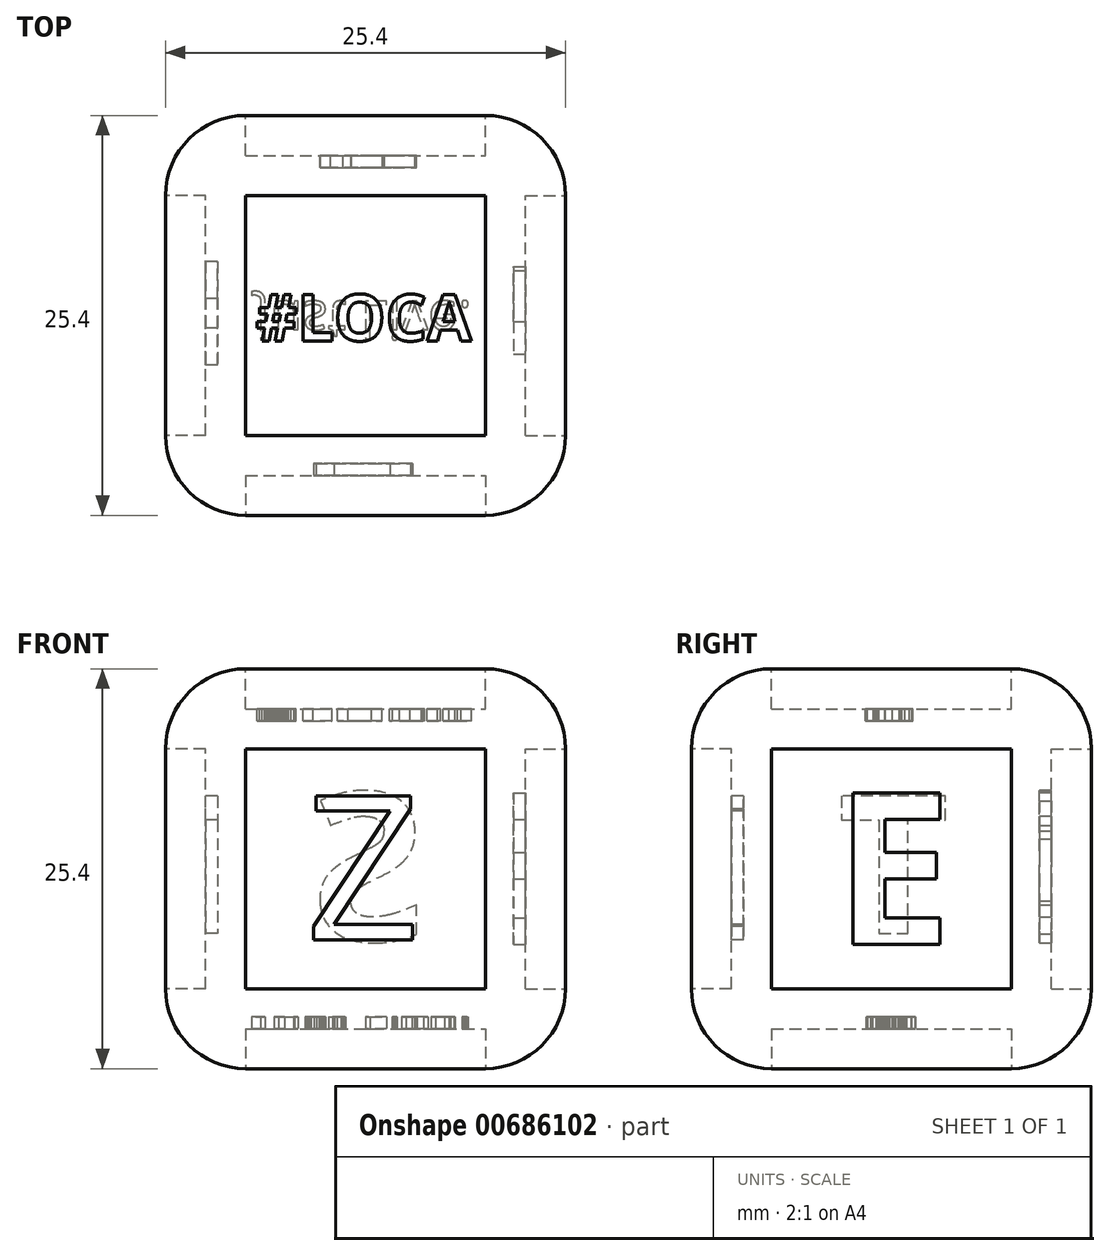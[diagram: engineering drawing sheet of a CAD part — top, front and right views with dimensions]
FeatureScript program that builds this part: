
annotation { "Feature Type Name" : "Feature", "Feature Type Description" : "" }
export const myFeature = defineFeature(function(context is Context, id is Id, definition is map)
    precondition{}
    {
        {
            var Q0;
            Q0=qCreatedBy(makeId("Front.planeOp"),FACE);
            var sketch = newSketch(context, id + "F0", { "sketchPlane" : qUnion([Q0])});
            skLineSegment(sketch, "E0.bottom", {"start": v(-12.7, -12.7) * mm, "end": v(12.7, -12.7) * mm});
            skLineSegment(sketch, "E0.top", {"start": v(-12.7, 12.7) * mm, "end": v(12.7, 12.7) * mm});
            skLineSegment(sketch, "E0.left", {"start": v(-12.7, -12.7) * mm, "end": v(-12.7, 12.7) * mm});
            skLineSegment(sketch, "E0.right", {"start": v(12.7, -12.7) * mm, "end": v(12.7, 12.7) * mm});
            skPoint(sketch, "E0.middle", {"position": v(0, 0) * mm});
            skSolve(sketch);
        }
        {
            var Q0;
            Q0=makeQuery(id+"F0.imprint","IMPRINT",FACE,{"disambiguationData":[TD([[makeQuery(id+"F0.imprint","IMPRINT",EDGE,{"derivedFrom":sQuery(id+"F0.wireOp",EDGE,"E0.bottom")}),1.0]])]});
            extrude(context, id + "F1", {"entities" : qUnion([Q0]), "depth" : 25.4 * mm, "offsetDistance" : 25.4 * mm});
        }
        {
            var Q0;
            Q0=makeQuery(id+"F1.opExtrude","CAP_FACE",FACE,{"disambiguationData":[OSD([sQuery(id+"F0.wireOp",EDGE,"E0.bottom"),sQuery(id+"F0.wireOp",EDGE,"E0.top"),sQuery(id+"F0.wireOp",EDGE,"E0.left"),sQuery(id+"F0.wireOp",EDGE,"E0.right")])],"isStart":false});
            var Q1;
            Q1=makeQuery(id+"F1.opExtrude","SWEPT_FACE",FACE,{"disambiguationData":[OSD([sQuery(id+"F0.wireOp",EDGE,"E0.right")])]});
            var Q2;
            Q2=makeQuery(id+"F1.opExtrude","SWEPT_FACE",FACE,{"disambiguationData":[OSD([sQuery(id+"F0.wireOp",EDGE,"E0.top")])]});
            var Q3;
            Q3=makeQuery(id+"F1.opExtrude","CAP_FACE",FACE,{"disambiguationData":[OSD([sQuery(id+"F0.wireOp",EDGE,"E0.bottom"),sQuery(id+"F0.wireOp",EDGE,"E0.top"),sQuery(id+"F0.wireOp",EDGE,"E0.left"),sQuery(id+"F0.wireOp",EDGE,"E0.right")])],"isStart":true});
            var Q4;
            Q4=makeQuery(id+"F1.opExtrude","SWEPT_FACE",FACE,{"disambiguationData":[OSD([sQuery(id+"F0.wireOp",EDGE,"E0.bottom")])]});
            var Q5;
            Q5=makeQuery(id+"F1.opExtrude","SWEPT_FACE",FACE,{"disambiguationData":[OSD([sQuery(id+"F0.wireOp",EDGE,"E0.left")])]});
            fillet(context, id + "F2", {"entities" : qUnion([Q0, Q1, Q2, Q3, Q4, Q5]), "radius" : 5.08 * mm, "tangentPropagation" : true, "allowEdgeOverflow" : false});
        }
        {
            var Q0;
            Q0=makeQuery(id+"F1.opExtrude","CAP_FACE",FACE,{"disambiguationData":[OSD([sQuery(id+"F0.wireOp",EDGE,"E0.bottom"),sQuery(id+"F0.wireOp",EDGE,"E0.top"),sQuery(id+"F0.wireOp",EDGE,"E0.left"),sQuery(id+"F0.wireOp",EDGE,"E0.right")])],"isStart":false});
            extrude(context, id + "F3", {"entities" : qUnion([Q0]), "operationType" : NewBodyOperationType.REMOVE, "oppositeDirection" : true, "depth" : 2.54 * mm, "offsetDistance" : 25.4 * mm});
        }
        {
            var Q0;
            Q0=makeQuery(id+"F1.opExtrude","SWEPT_FACE",FACE,{"disambiguationData":[OSD([sQuery(id+"F0.wireOp",EDGE,"E0.right")])]});
            extrude(context, id + "F4", {"entities" : qUnion([Q0]), "operationType" : NewBodyOperationType.REMOVE, "oppositeDirection" : true, "depth" : 2.54 * mm, "offsetDistance" : 25.4 * mm});
        }
        {
            var Q0;
            Q0=makeQuery(id+"F1.opExtrude","SWEPT_FACE",FACE,{"disambiguationData":[OSD([sQuery(id+"F0.wireOp",EDGE,"E0.top")])]});
            extrude(context, id + "F5", {"entities" : qUnion([Q0]), "operationType" : NewBodyOperationType.ADD, "depth" : 2.54 * mm, "offsetDistance" : 25.4 * mm});
        }
        {
            var Q0;
            Q0=makeQuery(id+"F5.opExtrude","CAP_FACE",FACE,{"disambiguationData":[OSD([sQuery(id+"F0.wireOp",EDGE,"E0.top")])],"isStart":false});
            extrude(context, id + "F6", {"entities" : qUnion([Q0]), "operationType" : NewBodyOperationType.REMOVE, "oppositeDirection" : true, "depth" : 5.08 * mm, "offsetDistance" : 25.4 * mm});
        }
        {
            var Q0;
            Q0=makeQuery(id+"F1.opExtrude","SWEPT_FACE",FACE,{"disambiguationData":[OSD([sQuery(id+"F0.wireOp",EDGE,"E0.bottom")])]});
            extrude(context, id + "F7", {"entities" : qUnion([Q0]), "operationType" : NewBodyOperationType.REMOVE, "oppositeDirection" : true, "depth" : 2.54 * mm, "offsetDistance" : 25.4 * mm});
        }
        {
            var Q0;
            Q0=makeQuery(id+"F1.opExtrude","CAP_FACE",FACE,{"disambiguationData":[OSD([sQuery(id+"F0.wireOp",EDGE,"E0.bottom"),sQuery(id+"F0.wireOp",EDGE,"E0.top"),sQuery(id+"F0.wireOp",EDGE,"E0.left"),sQuery(id+"F0.wireOp",EDGE,"E0.right")])],"isStart":true});
            extrude(context, id + "F8", {"entities" : qUnion([Q0]), "operationType" : NewBodyOperationType.ADD, "depth" : 2.54 * mm, "offsetDistance" : 25.4 * mm});
        }
        {
            var Q0;
            Q0=makeQuery(id+"F8.opExtrude","CAP_FACE",FACE,{"disambiguationData":[OSD([sQuery(id+"F0.wireOp",EDGE,"E0.bottom"),sQuery(id+"F0.wireOp",EDGE,"E0.top"),sQuery(id+"F0.wireOp",EDGE,"E0.left"),sQuery(id+"F0.wireOp",EDGE,"E0.right")])],"isStart":false});
            extrude(context, id + "F9", {"entities" : qUnion([Q0]), "operationType" : NewBodyOperationType.REMOVE, "oppositeDirection" : true, "depth" : 5.08 * mm, "offsetDistance" : 25.4 * mm});
        }
        {
            var Q0;
            Q0=makeQuery(id+"F1.opExtrude","SWEPT_FACE",FACE,{"disambiguationData":[OSD([sQuery(id+"F0.wireOp",EDGE,"E0.left")])]});
            extrude(context, id + "F10", {"entities" : qUnion([Q0]), "operationType" : NewBodyOperationType.REMOVE, "oppositeDirection" : true, "depth" : 2.54 * mm, "offsetDistance" : 25.4 * mm});
        }
        {
            var Q0;
            Q0=makeQuery(id+"F3.boolean.opBoolean","COPY",FACE,{"derivedFrom":makeQuery(id+"F3.opExtrude","CAP_FACE",FACE,{"disambiguationData":[OSD([sQuery(id+"F0.wireOp",EDGE,"E0.bottom"),sQuery(id+"F0.wireOp",EDGE,"E0.top"),sQuery(id+"F0.wireOp",EDGE,"E0.left"),sQuery(id+"F0.wireOp",EDGE,"E0.right")])],"isStart":false})});
            var sketch = newSketch(context, id + "F11", { "sketchPlane" : qUnion([Q0])});
            skText(sketch, "E1", { "text": "Z", "fontName": "OpenSans-Regular.ttf"});
            const initialGuessF11  = {"E1": [-0.00381, -0.00451, 1, 0, 0.00921]};
            skSetInitialGuess(sketch, initialGuessF11);
            skSolve(sketch);
        }
        {
            var Q0;
            Q0=makeQuery(id+"F11.imprint","IMPRINT",FACE,{"disambiguationData":[TD([[makeQuery(id+"F11.imprint","IMPRINT",EDGE,{"derivedFrom":sQuery(id+"F11.wireOp",EDGE,"E1.sketch_text.stroke-0")}),-1.0]])]});
            extrude(context, id + "F12", {"entities" : qUnion([Q0]), "operationType" : NewBodyOperationType.REMOVE, "oppositeDirection" : true, "depth" : 0.76 * mm, "offsetDistance" : 25.4 * mm});
        }
        {
            var Q0;
            Q0=makeQuery(id+"F4.boolean.opBoolean","COPY",FACE,{"derivedFrom":makeQuery(id+"F4.opExtrude","CAP_FACE",FACE,{"disambiguationData":[OSD([sQuery(id+"F0.wireOp",EDGE,"E0.right")])],"isStart":false})});
            var sketch = newSketch(context, id + "F13", { "sketchPlane" : qUnion([Q0])});
            skText(sketch, "E2", { "text": "E", "fontName": "OpenSans-Bold.ttf"});
            const initialGuessF13  = {"E2": [-0.01636, -0.0048, 1, 0, 0.0097]};
            skSetInitialGuess(sketch, initialGuessF13);
            skSolve(sketch);
        }
        {
            var Q0;
            Q0=makeQuery(id+"F13.imprint","IMPRINT",FACE,{"disambiguationData":[TD([[makeQuery(id+"F13.imprint","IMPRINT",EDGE,{"derivedFrom":sQuery(id+"F13.wireOp",EDGE,"E2.sketch_text.stroke-0")}),-1.0]])]});
            extrude(context, id + "F14", {"entities" : qUnion([Q0]), "operationType" : NewBodyOperationType.REMOVE, "oppositeDirection" : true, "depth" : 0.76 * mm, "offsetDistance" : 25.4 * mm});
        }
        {
            var Q0;
            Q0=makeQuery(id+"F9.boolean.opBoolean","COPY",FACE,{"derivedFrom":makeQuery(id+"F9.opExtrude","CAP_FACE",FACE,{"disambiguationData":[OSD([sQuery(id+"F0.wireOp",EDGE,"E0.bottom"),sQuery(id+"F0.wireOp",EDGE,"E0.top"),sQuery(id+"F0.wireOp",EDGE,"E0.left"),sQuery(id+"F0.wireOp",EDGE,"E0.right")])],"isStart":false})});
            var sketch = newSketch(context, id + "F15", { "sketchPlane" : qUnion([Q0])});
            skText(sketch, "E3", { "text": "S", "fontName": "OpenSans-Bold.ttf"});
            const initialGuessF15  = {"E3": [-0.00386, -0.00459, 1, 0, 0.00952]};
            skSetInitialGuess(sketch, initialGuessF15);
            skSolve(sketch);
        }
        {
            var Q0;
            Q0=makeQuery(id+"F15.imprint","IMPRINT",FACE,{"disambiguationData":[TD([[makeQuery(id+"F15.imprint","IMPRINT",EDGE,{"derivedFrom":sQuery(id+"F15.wireOp",EDGE,"E3.sketch_text.stroke-0")}),-1.0]])]});
            extrude(context, id + "F16", {"entities" : qUnion([Q0]), "operationType" : NewBodyOperationType.REMOVE, "oppositeDirection" : true, "depth" : 0.76 * mm, "offsetDistance" : 25.4 * mm});
        }
        {
            var Q0;
            Q0=makeQuery(id+"F10.boolean.opBoolean","COPY",FACE,{"derivedFrom":makeQuery(id+"F10.opExtrude","CAP_FACE",FACE,{"disambiguationData":[OSD([sQuery(id+"F0.wireOp",EDGE,"E0.left")])],"isStart":false})});
            var sketch = newSketch(context, id + "F17", { "sketchPlane" : qUnion([Q0])});
            skText(sketch, "E4", { "text": "T", "fontName": "OpenSans-Bold.ttf"});
            const initialGuessF17  = {"E4": [0.00903, -0.0041, 1, 0, 0.0088]};
            skSetInitialGuess(sketch, initialGuessF17);
            skSolve(sketch);
        }
        {
            var Q0;
            Q0=makeQuery(id+"F17.imprint","IMPRINT",FACE,{"disambiguationData":[TD([[makeQuery(id+"F17.imprint","IMPRINT",EDGE,{"derivedFrom":sQuery(id+"F17.wireOp",EDGE,"E4.sketch_text.stroke-0")}),-1.0]])]});
            extrude(context, id + "F18", {"entities" : qUnion([Q0]), "operationType" : NewBodyOperationType.REMOVE, "oppositeDirection" : true, "depth" : 0.76 * mm, "offsetDistance" : 25.4 * mm});
        }
        {
            var Q0;
            Q0=makeQuery(id+"F6.boolean.opBoolean","COPY",FACE,{"derivedFrom":makeQuery(id+"F6.opExtrude","CAP_FACE",FACE,{"disambiguationData":[OSD([sQuery(id+"F0.wireOp",EDGE,"E0.top")])],"isStart":false})});
            var sketch = newSketch(context, id + "F19", { "sketchPlane" : qUnion([Q0])});
            skText(sketch, "E5", { "text": "#LOCA", "fontName": "OpenSans-Bold.ttf"});
            const initialGuessF19  = {"E5": [-0.00698, -0.01432, 1, 0, 0.00296]};
            skSetInitialGuess(sketch, initialGuessF19);
            skSolve(sketch);
        }
        {
            var Q0;
            Q0 = qSketchRegion(id + "F19", true);
            extrude(context, id + "F20", {"entities" : qUnion([Q0]), "operationType" : NewBodyOperationType.REMOVE, "oppositeDirection" : true, "depth" : 0.76 * mm, "offsetDistance" : 25.4 * mm});
        }
        {
            var Q0;
            Q0=makeQuery(id+"F7.boolean.opBoolean","COPY",FACE,{"derivedFrom":makeQuery(id+"F7.opExtrude","CAP_FACE",FACE,{"disambiguationData":[OSD([sQuery(id+"F0.wireOp",EDGE,"E0.bottom")])],"isStart":false})});
            var sketch = newSketch(context, id + "F21", { "sketchPlane" : qUnion([Q0])});
            skText(sketch, "E6", { "text": "Just Live.", "fontName": "OpenSans-Regular.ttf"});
            const initialGuessF21  = {"E6": [-0.00698, 0.0118, 1, 0, 0.00243]};
            skSetInitialGuess(sketch, initialGuessF21);
            skSolve(sketch);
        }
        {
            var Q0;
            Q0 = qSketchRegion(id + "F21", true);
            extrude(context, id + "F22", {"entities" : qUnion([Q0]), "operationType" : NewBodyOperationType.REMOVE, "oppositeDirection" : true, "depth" : 0.76 * mm, "offsetDistance" : 25.4 * mm});
        }
    });
